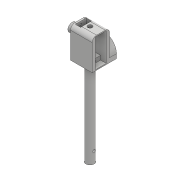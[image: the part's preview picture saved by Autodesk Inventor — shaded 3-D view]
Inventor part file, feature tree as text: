
AUTODESK INVENTOR PART (.ipt)
format: ipt  version: 2018 (Build 220112000, 112)  size: 275,456 bytes
history: native  units: mm
features: sketch x14, extrude x13, fillet x3, other x1
ambient origin geometry x8: Origin, YZ Plane, XZ Plane, XY Plane, X Axis, Y Axis, Z Axis, Center Point
bodies: Solid1 (feature_tree)
feature tree (31):
  extrude  "base"  Depth=20.0mm
  extrude  "attacher"  Depth=10.0mm
  fillet  "Fillet2"  Radius=9.5mm
  extrude  "hole_bar_rigify"  Depth=4.0mm
  extrude  "servo_place"  Depth=12.0mm TaperAngle=0.0deg
  extrude  "servo_place_2"  Depth=11.6mm
  extrude  "screw_holes"  Depth=23.2mm
  fillet  "Fillet3"  Radius=23.0mm
  extrude  "rot_axis"  Depth=4.7mm
  extrude  "rot_axis_hole"  Depth=1.9mm
  extrude  "cable_hole"  Depth=2.0mm
  fillet  "Fillet5"  Radius=2.0mm
  extrude  "cable_guide_1"  Depth=20.0mm
  sketch  "Sketch23"  dims[d93=5.0mm d94=11.0mm]
  sketch  "Sketch24"  dims[d95=10.0mm d96=8.0mm d97=0.0mm]
  extrude  "cable_guide_2"  Depth=11.0mm
  extrude  "cable_guide_3"  Depth=10.0mm TaperAngle=0.0deg
  other  "cable_guide_4"
  extrude  "Extrusion25"  Depth=10.0mm TaperAngle=0.0deg
  sketch  "Sketch1"  dims[d0=25.0mm d1=20.0mm]
  sketch  "Sketch4"  dims[d2=35.0mm d3=0.0mm d18=10.0mm d19=9.5mm]
  sketch  "Sketch5"  dims[d20=100.0mm d21=0.0mm d22=4.0mm]
  sketch  "Sketch15"  dims[d23=5.0mm d24=12.0mm d25=0.0mm]
  sketch  "Sketch16"  dims[d76=6.25mm d77=11.6mm]
  sketch  "Sketch17"  dims[d78=12.5mm d79=23.2mm d80=23.0mm d81=0.0mm]
  sketch  "Sketch18"  dims[d82=4.7mm d83=4.7mm]
  sketch  "Sketch20"  dims[d84=6.6mm d85=0.0mm d86=1.9mm]
  sketch  "Sketch21"  dims[d87=1.9mm d88=2.0mm d89=2.0mm]
  sketch  "Sketch22"  dims[d90=6.6mm d91=0.0mm d92=20.0mm]
  sketch  "Sketch25"  dims[d102=5.0mm d103=10.0mm d104=0.0mm]
  sketch  "Sketch26"  dims[d105=6.0mm d106=10.0mm d107=0.0mm d108=6.0mm d109=10.0mm d110=5.0mm d111=5.0mm d112=5.0mm d113=5.0mm d114=15.0mm d115=15.0mm d116=5.0mm d117=15.0mm d118=8.0mm d119=0.0mm d120=2.0mm d121=11.0mm d122=7.0mm d123=2.0mm d124=11.0mm d125=7.0mm d126=8.0mm d127=0.0mm d128=8.0mm d129=0.0mm d130=90.0deg d131=13.0mm d132=3.0mm d133=10.0mm d134=0.0mm]
